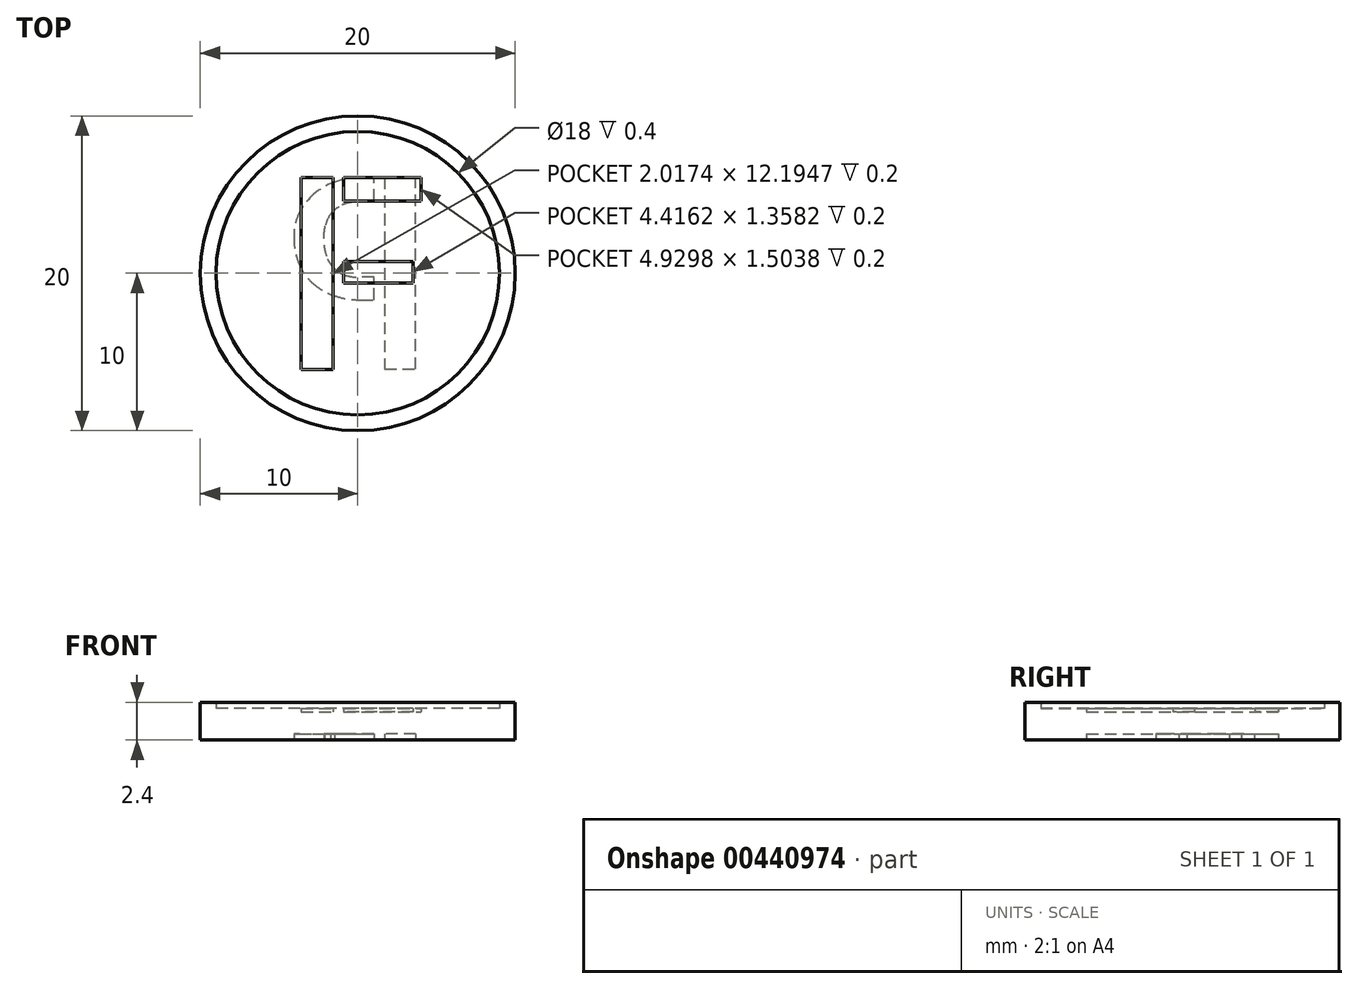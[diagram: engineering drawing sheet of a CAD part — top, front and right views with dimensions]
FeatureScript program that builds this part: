
annotation { "Feature Type Name" : "Feature", "Feature Type Description" : "" }
export const myFeature = defineFeature(function(context is Context, id is Id, definition is map)
    precondition{}
    {
        {
            var Q0;
            Q0=qCreatedBy(makeId("Top.planeOp"),FACE);
            var sketch = newSketch(context, id + "F0", { "sketchPlane" : qUnion([Q0])});
            skCircle(sketch, "E0", {"center": v(0, 0) * mm, "radius": 10 * mm});
            skText(sketch, "E1", { "text": "F", "fontName": "AllertaStencil-Regular.ttf"});
            const initialGuessF0  = {"E1": [-0.00517, -0.0061, 1, 0, 0.0122]};
            skSetInitialGuess(sketch, initialGuessF0);
            skSolve(sketch);
        }
        {
            var Q0;
            Q0=qSketchRegion(id+"F0",true);
            extrude(context, id + "F1", {"entities" : qUnion([Q0]), "depth" : 2 * mm});
        }
        {
            var Q0;
            Q0=makeQuery(id+"F0.imprint","IMPRINT",FACE,{"disambiguationData":[TD([[makeQuery(id+"F0.imprint","IMPRINT",EDGE,{"derivedFrom":sQuery(id+"F0.wireOp",EDGE,"E1.sketch_text.stroke-0")}),-1.0]])]});
            var Q1;
            Q1=makeQuery(id+"F0.imprint","IMPRINT",FACE,{"disambiguationData":[TD([[makeQuery(id+"F0.imprint","IMPRINT",EDGE,{"derivedFrom":sQuery(id+"F0.wireOp",EDGE,"E1.sketch_text.stroke-8")}),-1.0]])]});
            var Q2;
            Q2=makeQuery(id+"F0.imprint","IMPRINT",FACE,{"disambiguationData":[TD([[makeQuery(id+"F0.imprint","IMPRINT",EDGE,{"derivedFrom":sQuery(id+"F0.wireOp",EDGE,"E1.sketch_text.stroke-4")}),-1.0]])]});
            extrude(context, id + "F2", {"entities" : qUnion([Q0, Q1, Q2]), "operationType" : NewBodyOperationType.ADD, "depth" : 1.8 * mm});
        }
        {
            var Q0;
            Q0=makeQuery(id+"F1.opExtrude","CAP_FACE",FACE,{"disambiguationData":[OSD([sQuery(id+"F0.wireOp",EDGE,"E0"),sQuery(id+"F0.wireOp",EDGE,"E1.sketch_text.stroke-0"),sQuery(id+"F0.wireOp",EDGE,"E1.sketch_text.stroke-1"),sQuery(id+"F0.wireOp",EDGE,"E1.sketch_text.stroke-2"),sQuery(id+"F0.wireOp",EDGE,"E1.sketch_text.stroke-3"),sQuery(id+"F0.wireOp",EDGE,"E1.sketch_text.stroke-4"),sQuery(id+"F0.wireOp",EDGE,"E1.sketch_text.stroke-5")])],"isStart":false});
            var sketch = newSketch(context, id + "F3", { "sketchPlane" : qUnion([Q0])});
            skCircle(sketch, "E2.0.0", {"center": v(0, 0) * mm, "radius": 10 * mm});
            skCircle(sketch, "E3.0", {"center": v(0, 0) * mm, "radius": 9 * mm});
            skSolve(sketch);
        }
        {
            var Q0;
            Q0=makeQuery(id+"F3.imprint","IMPRINT",FACE,{"disambiguationData":[TD([[makeQuery(id+"F3.imprint","IMPRINT",EDGE,{"derivedFrom":sQuery(id+"F3.wireOp",EDGE,"E2.0.0")}),1.0]])]});
            extrude(context, id + "F4", {"entities" : qUnion([Q0]), "operationType" : NewBodyOperationType.ADD, "depth" : .4 * mm});
        }
        {
            var Q0;
            {var subQ0=sQuery(id+"F0.wireOp",EDGE,"E1.sketch_text.stroke-5");var subQ1=sQuery(id+"F0.wireOp",EDGE,"E1.sketch_text.stroke-4");var subQ2=sQuery(id+"F0.wireOp",EDGE,"E1.sketch_text.stroke-3");var subQ3=sQuery(id+"F0.wireOp",EDGE,"E1.sketch_text.stroke-2");var subQ4=sQuery(id+"F0.wireOp",EDGE,"E1.sketch_text.stroke-1");var subQ5=sQuery(id+"F0.wireOp",EDGE,"E1.sketch_text.stroke-0");Q0=makeQuery(id+"F2.boolean.opBoolean","MERGE",FACE,{"derivedFrom":[makeQuery(id+"F1.opExtrude","CAP_FACE",FACE,{"disambiguationData":[OSD([sQuery(id+"F0.wireOp",EDGE,"E0"),subQ5,subQ4,subQ3,subQ2,subQ1,subQ0])],"isStart":true}),makeQuery(id+"F2.opExtrude","CAP_FACE",FACE,{"disambiguationData":[OSD([subQ5,subQ4,subQ3,subQ2,subQ1,subQ0])],"isStart":true})]});}
            var sketch = newSketch(context, id + "F5", { "sketchPlane" : qUnion([Q0])});
            skCircle(sketch, "E4.0", {"center": v(0, 0) * mm, "radius": 9 * mm});
            skText(sketch, "E5", { "text": "P", "fontName": "AllertaStencil-Regular.ttf"});
            const initialGuessF5  = {"E5": [0.00519, 0.00609, -1, 0, 0.01218]};
            skSetInitialGuess(sketch, initialGuessF5);
            skSolve(sketch);
        }
        {
            var Q0;
            Q0=makeQuery(id+"F5.imprint","IMPRINT",FACE,{"disambiguationData":[TD([[makeQuery(id+"F5.imprint","IMPRINT",EDGE,{"derivedFrom":sQuery(id+"F5.wireOp",EDGE,"E5.sketch_text.stroke-0")}),-1.0]])]});
            var Q1;
            Q1=makeQuery(id+"F5.imprint","IMPRINT",FACE,{"disambiguationData":[TD([[makeQuery(id+"F5.imprint","IMPRINT",EDGE,{"derivedFrom":sQuery(id+"F5.wireOp",EDGE,"E5.sketch_text.stroke-4")}),-1.0]])]});
            extrude(context, id + "F6", {"entities" : qUnion([Q0, Q1]), "operationType" : NewBodyOperationType.REMOVE, "oppositeDirection" : true, "depth" : .4 * mm});
        }
        {
            var Q0;
            Q0=makeQuery(id+"F2.opExtrude","CAP_FACE",FACE,{"disambiguationData":[OSD([sQuery(id+"F0.wireOp",EDGE,"E1.sketch_text.stroke-0"),sQuery(id+"F0.wireOp",EDGE,"E1.sketch_text.stroke-1"),sQuery(id+"F0.wireOp",EDGE,"E1.sketch_text.stroke-2"),sQuery(id+"F0.wireOp",EDGE,"E1.sketch_text.stroke-3"),sQuery(id+"F0.wireOp",EDGE,"E1.sketch_text.stroke-4"),sQuery(id+"F0.wireOp",EDGE,"E1.sketch_text.stroke-5")])],"isStart":false});
            var Q1;
            Q1=makeQuery(id+"F2.opExtrude","CAP_FACE",FACE,{"disambiguationData":[OSD([sQuery(id+"F0.wireOp",EDGE,"E1.sketch_text.stroke-8"),sQuery(id+"F0.wireOp",EDGE,"E1.sketch_text.stroke-9"),sQuery(id+"F0.wireOp",EDGE,"E1.sketch_text.stroke-10"),sQuery(id+"F0.wireOp",EDGE,"E1.sketch_text.stroke-11")])],"isStart":false});
            var Q2;
            Q2=makeQuery(id+"F2.opExtrude","CAP_FACE",FACE,{"disambiguationData":[OSD([sQuery(id+"F0.wireOp",EDGE,"E1.sketch_text.stroke-4"),sQuery(id+"F0.wireOp",EDGE,"E1.sketch_text.stroke-5"),sQuery(id+"F0.wireOp",EDGE,"E1.sketch_text.stroke-6"),sQuery(id+"F0.wireOp",EDGE,"E1.sketch_text.stroke-7")])],"isStart":false});
            extrude(context, id + "F7", {"entities" : qUnion([Q0, Q1, Q2]), "depth" : .2 * mm});
        }
    });
